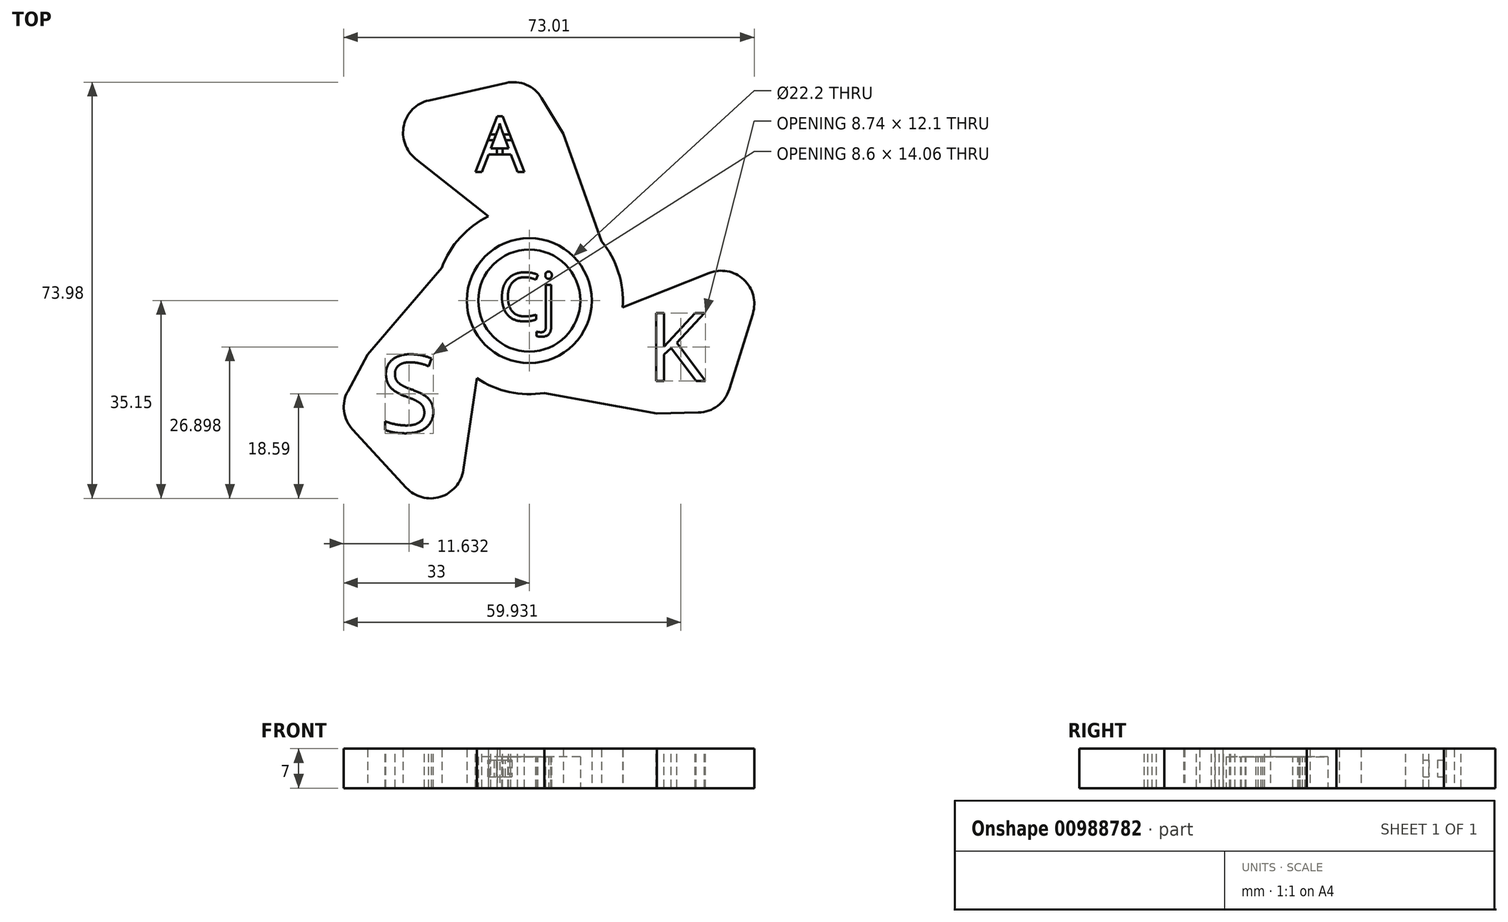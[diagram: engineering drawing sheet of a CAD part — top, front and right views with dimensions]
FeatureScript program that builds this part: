
annotation { "Feature Type Name" : "Feature", "Feature Type Description" : "" }
export const myFeature = defineFeature(function(context is Context, id is Id, definition is map)
    precondition{}
    {
        {
            var Q0;
            Q0=qCreatedBy(makeId("Top.planeOp"),FACE);
            var sketch = newSketch(context, id + "F0", { "sketchPlane" : qUnion([Q0])});
            skCircle(sketch, "E0", {"center": v(0, 0) * mm, "radius": 16.64 * mm});
            skCircle(sketch, "E1", {"center": v(0, 0) * mm, "radius": 11.1 * mm});
            skLineSegment(sketch, "E2", {"start": v(-7.28, 14.96) * mm, "end": v(-20.22, 25.23) * mm});
            skLineSegment(sketch, "E3", {"start": v(-17.86, 35.58) * mm, "end": v(-4.13, 38.69) * mm});
            skArc(sketch, "E4.filletArc", {"start": v(-17.86, 35.58) * mm, "mid": v(-22.3, 31.15) * mm, "end": v(-20.22, 25.23) * mm});
            skLineSegment(sketch, "E5", {"start": v(2.2, 36) * mm, "end": v(6.04, 29.68) * mm});
            skPoint(sketch, "E6.visualSharp", {"position": v(0, 39.62) * mm});
            skArc(sketch, "E6.filletArc", {"start": v(2.2, 36) * mm, "mid": v(-0.53, 38.36) * mm, "end": v(-4.13, 38.69) * mm});
            skLineSegment(sketch, "E7", {"start": v(6.04, 29.68) * mm, "end": v(12.87, 10.54) * mm});
            skArc(sketch, "E8.1.0", {"start": v(-21.89, -33.26) * mm, "mid": v(-15.83, -34.89) * mm, "end": v(-11.74, -30.12) * mm});
            skLineSegment(sketch, "E8.1.1", {"start": v(-21.89, -33.26) * mm, "end": v(-31.44, -22.92) * mm});
            skArc(sketch, "E8.1.2", {"start": v(-32.28, -16.1) * mm, "mid": v(-32.96, -19.64) * mm, "end": v(-31.44, -22.92) * mm});
            skLineSegment(sketch, "E8.1.3", {"start": v(-28.72, -9.61) * mm, "end": v(-15.57, 5.87) * mm});
            skLineSegment(sketch, "E8.1.4", {"start": v(-9.31, -13.78) * mm, "end": v(-11.74, -30.12) * mm});
            skLineSegment(sketch, "E8.1.5", {"start": v(-32.28, -16.1) * mm, "end": v(-28.72, -9.61) * mm});
            skArc(sketch, "E8.2.0", {"start": v(39.74, -2.33) * mm, "mid": v(38.13, 3.74) * mm, "end": v(31.96, 4.9) * mm});
            skLineSegment(sketch, "E8.2.1", {"start": v(39.74, -2.33) * mm, "end": v(35.57, -15.76) * mm});
            skArc(sketch, "E8.2.2", {"start": v(30.08, -19.9) * mm, "mid": v(33.49, -18.72) * mm, "end": v(35.57, -15.76) * mm});
            skLineSegment(sketch, "E8.2.3", {"start": v(22.69, -20.07) * mm, "end": v(2.7, -16.42) * mm});
            skLineSegment(sketch, "E8.2.4", {"start": v(16.6, -1.17) * mm, "end": v(31.96, 4.9) * mm});
            skLineSegment(sketch, "E8.2.5", {"start": v(30.08, -19.9) * mm, "end": v(22.69, -20.07) * mm});
            skSolve(sketch);
        }
        {
            var Q0;
            Q0 = qSketchRegion(id + "F0", true);
            extrude(context, id + "F1", {"entities" : qUnion([Q0]), "depth" : 7 * mm, "offsetDistance" : 25.4 * mm});
        }
        {
            var Q0;
            Q0=makeQuery(id+"F1.opExtrude","CAP_FACE",FACE,{"disambiguationData":[OSD([sQuery(id+"F0.wireOp",EDGE,"E0"),sQuery(id+"F0.wireOp",EDGE,"E1"),sQuery(id+"F0.wireOp",EDGE,"E2"),sQuery(id+"F0.wireOp",EDGE,"E3"),sQuery(id+"F0.wireOp",EDGE,"E4.filletArc"),sQuery(id+"F0.wireOp",EDGE,"E5"),sQuery(id+"F0.wireOp",EDGE,"E6.filletArc"),sQuery(id+"F0.wireOp",EDGE,"E7"),sQuery(id+"F0.wireOp",EDGE,"E8.1.0"),sQuery(id+"F0.wireOp",EDGE,"E8.1.1"),sQuery(id+"F0.wireOp",EDGE,"E8.1.2"),sQuery(id+"F0.wireOp",EDGE,"E8.1.3"),sQuery(id+"F0.wireOp",EDGE,"E8.1.4"),sQuery(id+"F0.wireOp",EDGE,"E8.1.5"),sQuery(id+"F0.wireOp",EDGE,"E8.2.0"),sQuery(id+"F0.wireOp",EDGE,"E8.2.1"),sQuery(id+"F0.wireOp",EDGE,"E8.2.2"),sQuery(id+"F0.wireOp",EDGE,"E8.2.3"),sQuery(id+"F0.wireOp",EDGE,"E8.2.4"),sQuery(id+"F0.wireOp",EDGE,"E8.2.5")])],"isStart":false});
            var sketch = newSketch(context, id + "F2", { "sketchPlane" : qUnion([Q0])});
            skText(sketch, "E9", { "text": "K", "fontName": "OpenSans-Regular.ttf"});
            const initialGuessF2  = {"E9": [0.0209, -0.0143, 1, 0, 0.0122]};
            skSetInitialGuess(sketch, initialGuessF2);
            skSolve(sketch);
        }
        {
            var Q0;
            Q0 = qSketchRegion(id + "F2", true);
            extrude(context, id + "F3", {"entities" : qUnion([Q0]), "operationType" : NewBodyOperationType.REMOVE, "oppositeDirection" : true, "depth" : 25.4 * mm, "offsetDistance" : 25.4 * mm});
        }
        {
            var Q0;
            Q0=makeQuery(id+"F1.opExtrude","CAP_FACE",FACE,{"disambiguationData":[OSD([sQuery(id+"F0.wireOp",EDGE,"E0"),sQuery(id+"F0.wireOp",EDGE,"E1"),sQuery(id+"F0.wireOp",EDGE,"E2"),sQuery(id+"F0.wireOp",EDGE,"E3"),sQuery(id+"F0.wireOp",EDGE,"E4.filletArc"),sQuery(id+"F0.wireOp",EDGE,"E5"),sQuery(id+"F0.wireOp",EDGE,"E6.filletArc"),sQuery(id+"F0.wireOp",EDGE,"E7"),sQuery(id+"F0.wireOp",EDGE,"E8.1.0"),sQuery(id+"F0.wireOp",EDGE,"E8.1.1"),sQuery(id+"F0.wireOp",EDGE,"E8.1.2"),sQuery(id+"F0.wireOp",EDGE,"E8.1.3"),sQuery(id+"F0.wireOp",EDGE,"E8.1.4"),sQuery(id+"F0.wireOp",EDGE,"E8.1.5"),sQuery(id+"F0.wireOp",EDGE,"E8.2.0"),sQuery(id+"F0.wireOp",EDGE,"E8.2.1"),sQuery(id+"F0.wireOp",EDGE,"E8.2.2"),sQuery(id+"F0.wireOp",EDGE,"E8.2.3"),sQuery(id+"F0.wireOp",EDGE,"E8.2.4"),sQuery(id+"F0.wireOp",EDGE,"E8.2.5")])],"isStart":false});
            var sketch = newSketch(context, id + "F4", { "sketchPlane" : qUnion([Q0])});
            skText(sketch, "E10", { "text": "A", "fontName": "OpenSans-Regular.ttf"});
            const initialGuessF4  = {"E10": [-0.0096, 0.02288, 1, 0, 0.00991]};
            skSetInitialGuess(sketch, initialGuessF4);
            skSolve(sketch);
        }
        {
            var Q0;
            Q0 = qSketchRegion(id + "F4", true);
            extrude(context, id + "F5", {"entities" : qUnion([Q0]), "operationType" : NewBodyOperationType.REMOVE, "oppositeDirection" : true, "depth" : 25.4 * mm, "offsetDistance" : 25.4 * mm});
        }
        {
            var Q0;
            {var subQ0=sQuery(id+"F0.wireOp",EDGE,"E8.2.4");var subQ1=sQuery(id+"F0.wireOp",EDGE,"E8.2.3");var subQ2=sQuery(id+"F0.wireOp",EDGE,"E8.2.2");var subQ3=sQuery(id+"F0.wireOp",EDGE,"E8.2.1");var subQ4=sQuery(id+"F0.wireOp",EDGE,"E8.2.0");var subQ5=sQuery(id+"F0.wireOp",EDGE,"E8.1.5");var subQ6=sQuery(id+"F0.wireOp",EDGE,"E8.1.4");var subQ7=sQuery(id+"F0.wireOp",EDGE,"E8.1.3");var subQ8=sQuery(id+"F0.wireOp",EDGE,"E8.1.2");var subQ9=sQuery(id+"F0.wireOp",EDGE,"E8.1.1");var subQ10=sQuery(id+"F0.wireOp",EDGE,"E8.1.0");var subQ11=sQuery(id+"F0.wireOp",EDGE,"E7");var subQ12=sQuery(id+"F0.wireOp",EDGE,"E0");var subQ13=sQuery(id+"F0.wireOp",EDGE,"E1");var subQ14=sQuery(id+"F0.wireOp",EDGE,"E8.2.5");var subQ15=sQuery(id+"F0.wireOp",EDGE,"E2");var subQ16=sQuery(id+"F0.wireOp",EDGE,"E3");var subQ17=sQuery(id+"F0.wireOp",EDGE,"E4.filletArc");var subQ18=sQuery(id+"F0.wireOp",EDGE,"E5");var subQ19=sQuery(id+"F0.wireOp",EDGE,"E6.filletArc");Q0=makeQuery(id+"F5.boolean.opBoolean","SPLIT",FACE,{"disambiguationData":[TD([makeQuery(id+"F1.opExtrude","SWEPT_FACE",FACE,{"disambiguationData":[OSD([subQ13])]})])],"derivedFrom":makeQuery(id+"F1.opExtrude","CAP_FACE",FACE,{"disambiguationData":[OSD([subQ12,subQ13,subQ15,subQ16,subQ17,subQ18,subQ19,subQ11,subQ10,subQ9,subQ8,subQ7,subQ6,subQ5,subQ4,subQ3,subQ2,subQ1,subQ0,subQ14])],"isStart":false})});}
            var sketch = newSketch(context, id + "F6", { "sketchPlane" : qUnion([Q0])});
            skText(sketch, "E11", { "text": "S\n", "fontName": "OpenSans-Regular.ttf"});
            skPoint(sketch, "E11.firstSnap0", {"position": v(-15.83, -34.89) * mm});
            skPoint(sketch, "E11.secondSnap0", {"position": v(-26.66, -28.09) * mm});
            const initialGuessF6  = {"E11": [-0.02666, -0.0234, 1, 0, 0.01379]};
            skSetInitialGuess(sketch, initialGuessF6);
            skSolve(sketch);
        }
        {
            var Q0;
            Q0 = qSketchRegion(id + "F6", true);
            extrude(context, id + "F7", {"entities" : qUnion([Q0]), "operationType" : NewBodyOperationType.REMOVE, "oppositeDirection" : true, "depth" : 25.4 * mm, "offsetDistance" : 25.4 * mm});
        }
        {
            var Q0;
            Q0=qCreatedBy(makeId("Top.planeOp"),FACE);
            var sketch = newSketch(context, id + "F8", { "sketchPlane" : qUnion([Q0])});
            skCircle(sketch, "E12", {"center": v(0, 0) * mm, "radius": 9.07 * mm});
            skSolve(sketch);
        }
        {
            var Q0;
            Q0 = qSketchRegion(id + "F8", true);
            extrude(context, id + "F9", {"entities" : qUnion([Q0]), "depth" : 5.6 * mm, "offsetDistance" : 25.4 * mm});
        }
        {
            var Q0;
            Q0=makeQuery(id+"F9.opExtrude","CAP_FACE",FACE,{"disambiguationData":[OSD([sQuery(id+"F8.wireOp",EDGE,"E12")])],"isStart":false});
            var sketch = newSketch(context, id + "F10", { "sketchPlane" : qUnion([Q0])});
            skText(sketch, "E13", { "text": "Cj", "fontName": "OpenSans-Regular.ttf"});
            const initialGuessF10  = {"E13": [-0.00559, -0.00358, 1, 0, 0.00857]};
            skSetInitialGuess(sketch, initialGuessF10);
            skSolve(sketch);
        }
        {
            var Q0;
            Q0 = qSketchRegion(id + "F10", true);
            extrude(context, id + "F11", {"entities" : qUnion([Q0]), "operationType" : NewBodyOperationType.REMOVE, "oppositeDirection" : true, "depth" : 25.4 * mm, "offsetDistance" : 25.4 * mm});
        }
        {
            var Q0;
            Q0=qCreatedBy(makeId("Top.planeOp"),FACE);
            cPlane(context, id + "F12", {"entities" : qUnion([Q0]), "cplaneType" : CPlaneType.OFFSET, "offset" : 2 * mm, "width" : 150 * mm, "height" : 150 * mm});
        }
        {
            var Q0;
            Q0=qCreatedBy(id+"F12.planeOp",FACE);
            var sketch = newSketch(context, id + "F13", { "sketchPlane" : qUnion([Q0])});
            skLineSegment(sketch, "E14.bottom", {"start": v(-8.24, 29.54) * mm, "end": v(-2.24, 29.54) * mm});
            skLineSegment(sketch, "E14.top", {"start": v(-8.24, 28.54) * mm, "end": v(-2.24, 28.54) * mm});
            skLineSegment(sketch, "E14.left", {"start": v(-8.24, 29.54) * mm, "end": v(-8.24, 28.54) * mm});
            skLineSegment(sketch, "E14.right", {"start": v(-2.24, 29.54) * mm, "end": v(-2.24, 28.54) * mm});
            skLineSegment(sketch, "E15.bottom", {"start": v(-5.74, 25.04) * mm, "end": v(-4.74, 25.04) * mm});
            skLineSegment(sketch, "E15.top", {"start": v(-5.74, 28.04) * mm, "end": v(-4.74, 28.04) * mm});
            skLineSegment(sketch, "E15.left", {"start": v(-5.74, 25.04) * mm, "end": v(-5.74, 28.04) * mm});
            skLineSegment(sketch, "E15.right", {"start": v(-4.74, 25.04) * mm, "end": v(-4.74, 28.04) * mm});
            skSolve(sketch);
        }
        {
            var Q0;
            Q0 = qSketchRegion(id + "F13", true);
            extrude(context, id + "F14", {"entities" : qUnion([Q0]), "operationType" : NewBodyOperationType.ADD, "depth" : 3 * mm, "offsetDistance" : 25 * mm});
        }
    });
